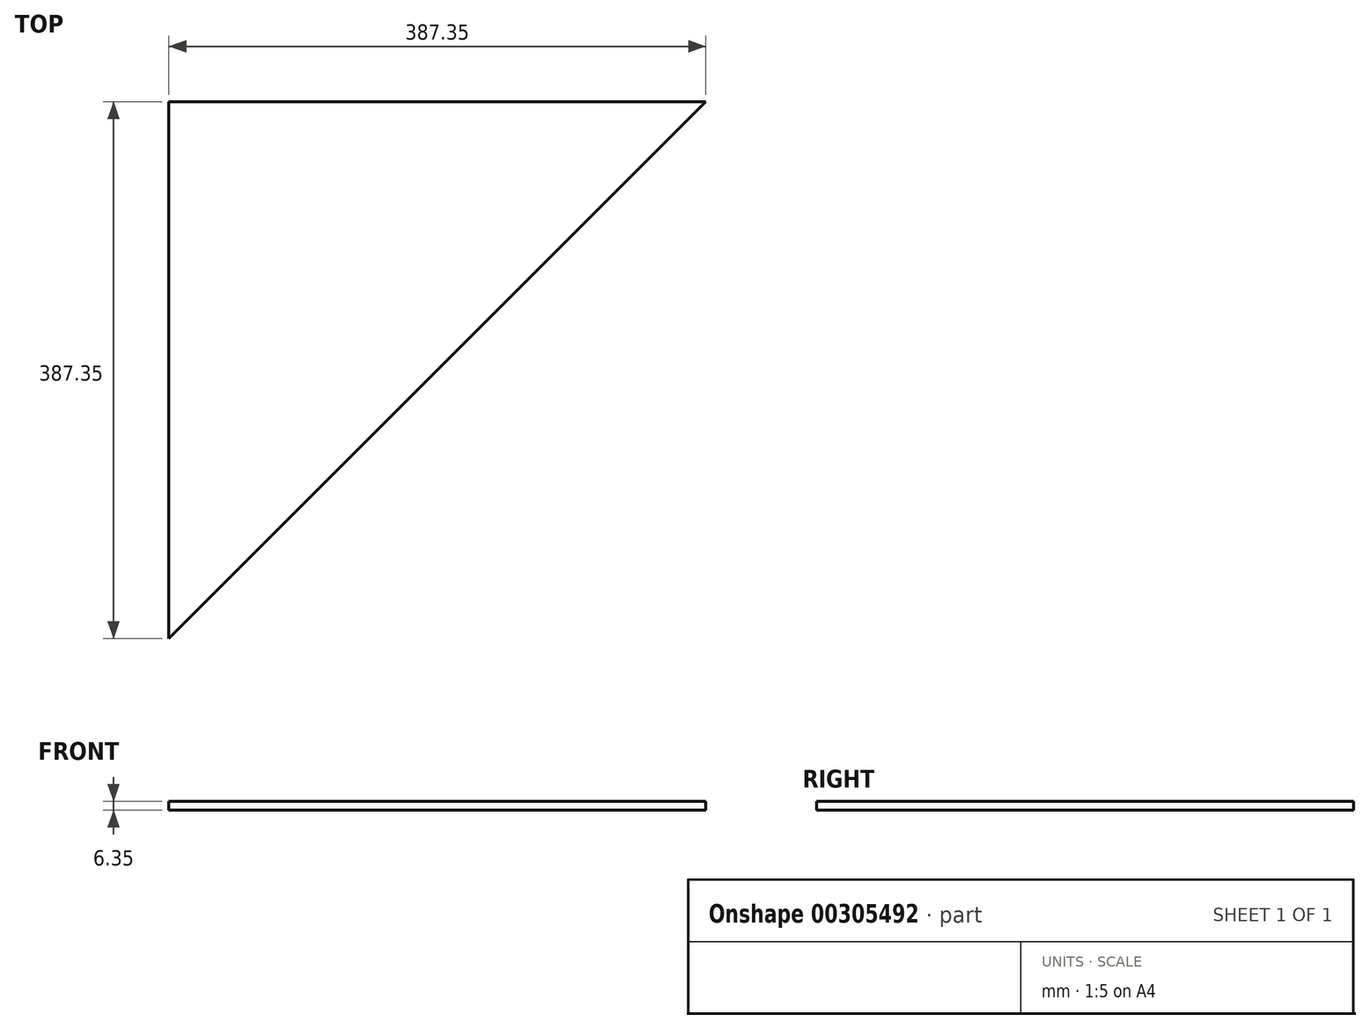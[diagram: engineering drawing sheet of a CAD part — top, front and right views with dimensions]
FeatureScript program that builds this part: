
annotation { "Feature Type Name" : "Feature", "Feature Type Description" : "" }
export const myFeature = defineFeature(function(context is Context, id is Id, definition is map)
    precondition{}
    {
        {
            var Q0;
            Q0=qCreatedBy(makeId("Top.planeOp"),FACE);
            var sketch = newSketch(context, id + "F0", { "sketchPlane" : qUnion([Q0])});
            skLineSegment(sketch, "E0.bottom", {"start": v(-184.94, 215.81) * mm, "end": v(202.41, 215.81) * mm});
            skLineSegment(sketch, "E0.left", {"start": v(-184.94, 215.81) * mm, "end": v(-184.94, -171.54) * mm});
            skLineSegment(sketch, "E1", {"start": v(-184.94, -171.54) * mm, "end": v(202.41, 215.81) * mm});
            skSolve(sketch);
        }
        {
            var Q0;
            Q0=makeQuery(id+"F0.imprint","IMPRINT",FACE,{"disambiguationData":[TD([[makeQuery(id+"F0.imprint","IMPRINT",EDGE,{"derivedFrom":sQuery(id+"F0.wireOp",EDGE,"E0.bottom")}),-1.0]])]});
            extrude(context, id + "F1", {"entities" : qUnion([Q0]), "depth" : 6.35 * mm});
        }
    });
